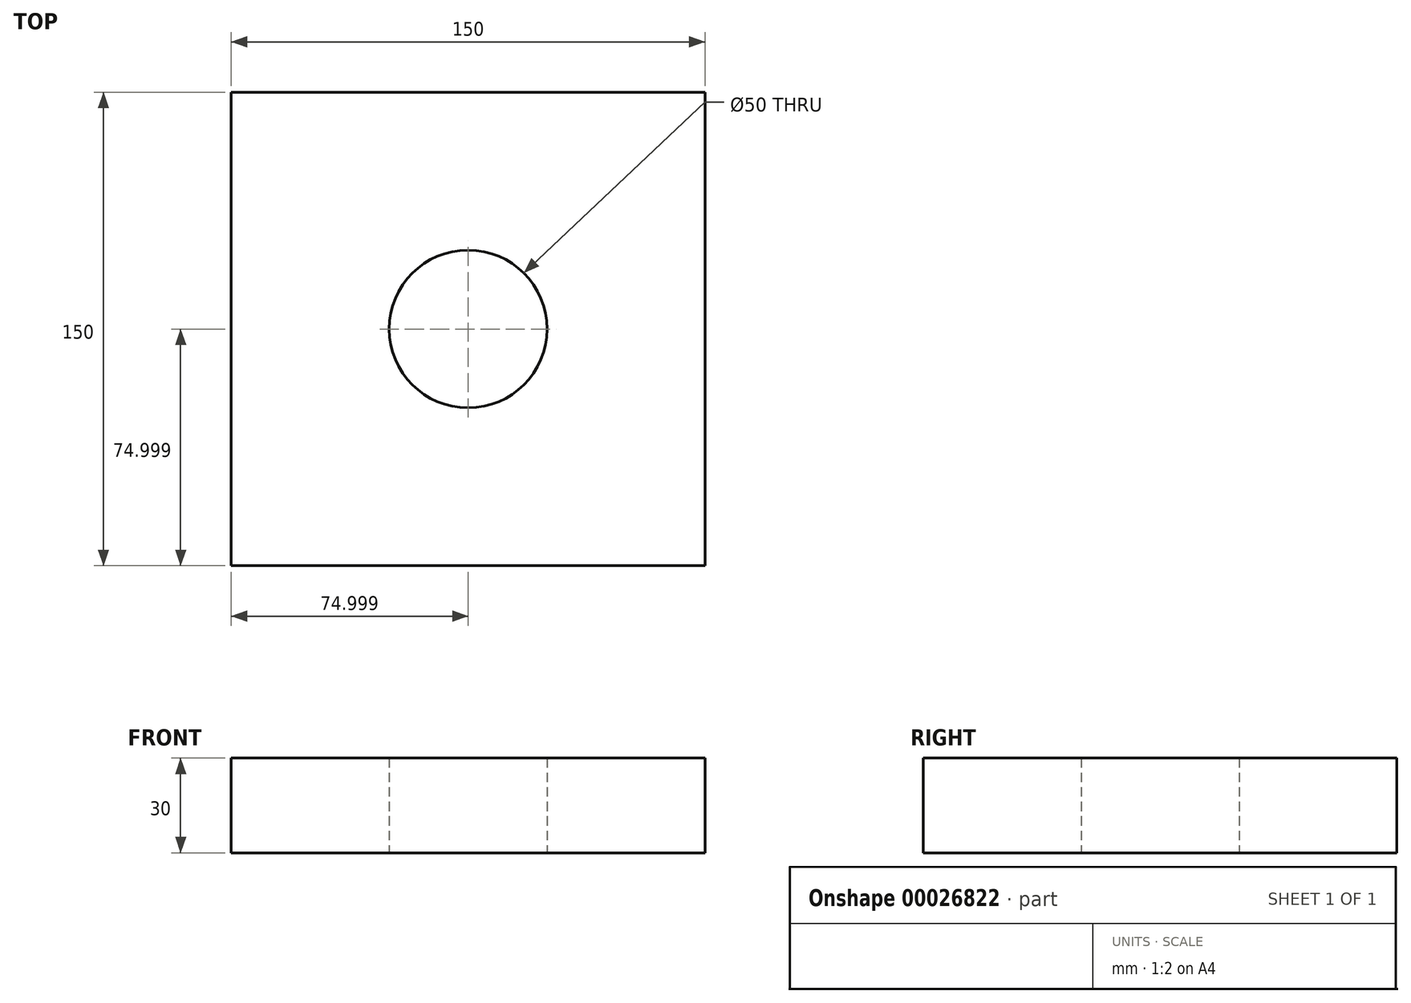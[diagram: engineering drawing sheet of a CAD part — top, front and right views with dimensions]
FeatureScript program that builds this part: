
annotation { "Feature Type Name" : "Feature", "Feature Type Description" : "" }
export const myFeature = defineFeature(function(context is Context, id is Id, definition is map)
    precondition{}
    {
        {
            var Q0;
            Q0=qCreatedBy(makeId("Top.planeOp"),FACE);
            var sketch = newSketch(context, id + "F0", { "sketchPlane" : qUnion([Q0])});
            skLineSegment(sketch, "E0.bottom", {"start": v(-54.45, 67.58) * mm, "end": v(95.55, 67.58) * mm});
            skLineSegment(sketch, "E0.top", {"start": v(-54.45, -82.42) * mm, "end": v(95.55, -82.42) * mm});
            skLineSegment(sketch, "E0.left", {"start": v(-54.45, 67.58) * mm, "end": v(-54.45, -82.42) * mm});
            skLineSegment(sketch, "E0.right", {"start": v(95.55, 67.58) * mm, "end": v(95.55, -82.42) * mm});
            skLineSegment(sketch, "E1", {"start": v(-54.45, 67.58) * mm, "end": v(20.55, 67.58) * mm});
            skLineSegment(sketch, "E2", {"start": v(-54.45, -82.42) * mm, "end": v(-4.45, -82.42) * mm});
            skLineSegment(sketch, "E3", {"start": v(20.55, 67.58) * mm, "end": v(20.55, -33.59) * mm});
            skLineSegment(sketch, "E4", {"start": v(-54.45, 67.58) * mm, "end": v(-54.45, -7.42) * mm});
            skLineSegment(sketch, "E5", {"start": v(95.55, 67.58) * mm, "end": v(95.55, -7.42) * mm});
            skLineSegment(sketch, "E6", {"start": v(-54.45, -7.42) * mm, "end": v(95.55, -7.42) * mm});
            skCircle(sketch, "E7", {"center": v(20.55, -7.42) * mm, "radius": 25 * mm});
            skSolve(sketch);
        }
        {
            var Q0;
            {var subQ6=sQuery(id+"F0.wireOp",EDGE,"E0.bottom");Q0=makeQuery(id+"F0.imprint","IMPRINT",FACE,{"disambiguationData":[TD([[makeQuery(id+"F0.imprint","IMPRINT",EDGE,{"derivedFrom":subQ6}),-1.0]])]});}
            var Q1;
            {var subQ6=sQuery(id+"F0.wireOp",EDGE,"E0.top");Q1=makeQuery(id+"F0.imprint","IMPRINT",FACE,{"disambiguationData":[TD([[makeQuery(id+"F0.imprint","IMPRINT",EDGE,{"derivedFrom":subQ6}),1.0]])]});}
            var Q2;
            {var subQ5=sQuery(id+"F0.wireOp",EDGE,"E0.left");Q2=makeQuery(id+"F0.imprint","IMPRINT",FACE,{"disambiguationData":[TD([[makeQuery(id+"F0.imprint","IMPRINT",EDGE,{"derivedFrom":subQ5}),1.0]])]});}
            var Q3;
            {var subQ6=sQuery(id+"F0.wireOp",EDGE,"E1");Q3=makeQuery(id+"F0.imprint","IMPRINT",FACE,{"disambiguationData":[TD([[makeQuery(id+"F0.imprint","IMPRINT",EDGE,{"derivedFrom":subQ6}),-1.0]])]});}
            extrude(context, id + "F1", {"entities" : qUnion([Q0, Q1, Q2, Q3]), "depth" : 30 * mm});
        }
    });
